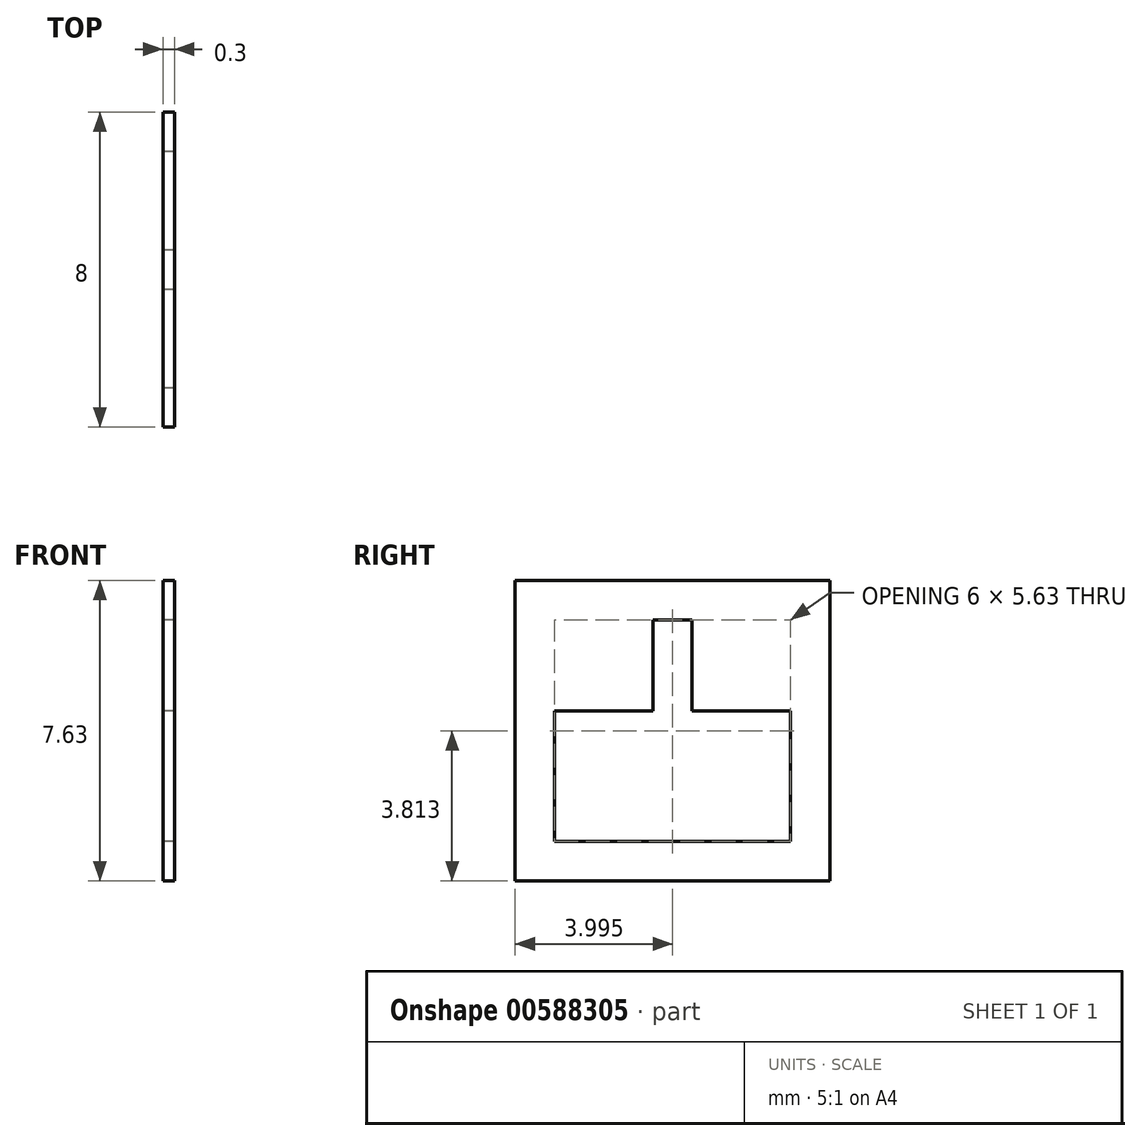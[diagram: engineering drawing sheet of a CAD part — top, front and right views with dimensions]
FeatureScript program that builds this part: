
annotation { "Feature Type Name" : "Feature", "Feature Type Description" : "" }
export const myFeature = defineFeature(function(context is Context, id is Id, definition is map)
    precondition{}
    {
        {
            var Q0;
            Q0=qCreatedBy(makeId("Right.planeOp"),FACE);
            var sketch = newSketch(context, id + "F0", { "sketchPlane" : qUnion([Q0])});
            skLineSegment(sketch, "E0.bottom", {"start": v(-15.22, -11.44) * mm, "end": v(-7.22, -11.44) * mm});
            skLineSegment(sketch, "E0.top", {"start": v(-15.22, -19.07) * mm, "end": v(-7.22, -19.07) * mm});
            skLineSegment(sketch, "E0.left", {"start": v(-15.22, -11.44) * mm, "end": v(-15.22, -19.07) * mm});
            skLineSegment(sketch, "E0.right", {"start": v(-7.22, -11.44) * mm, "end": v(-7.22, -19.07) * mm});
            skLineSegment(sketch, "E1.0", {"start": v(-14.22, -12.44) * mm, "end": v(-8.22, -12.44) * mm});
            skLineSegment(sketch, "E1.1", {"start": v(-14.22, -12.44) * mm, "end": v(-14.22, -18.07) * mm});
            skLineSegment(sketch, "E1.2", {"start": v(-14.22, -18.07) * mm, "end": v(-8.22, -18.07) * mm});
            skLineSegment(sketch, "E1.3", {"start": v(-8.22, -12.44) * mm, "end": v(-8.22, -18.07) * mm});
            skLineSegment(sketch, "E2.bottom", {"start": v(-14.22, -12.44) * mm, "end": v(-11.72, -12.44) * mm});
            skLineSegment(sketch, "E2.top", {"start": v(-14.22, -14.75) * mm, "end": v(-11.72, -14.75) * mm});
            skLineSegment(sketch, "E2.left", {"start": v(-14.22, -12.44) * mm, "end": v(-14.22, -14.75) * mm});
            skLineSegment(sketch, "E2.right", {"start": v(-11.72, -12.44) * mm, "end": v(-11.72, -14.75) * mm});
            skLineSegment(sketch, "E3.bottom", {"start": v(-14.22, -18.07) * mm, "end": v(-11.72, -18.07) * mm});
            skLineSegment(sketch, "E3.top", {"start": v(-14.22, -15.76) * mm, "end": v(-11.72, -15.76) * mm});
            skLineSegment(sketch, "E3.left", {"start": v(-14.22, -18.07) * mm, "end": v(-14.22, -15.76) * mm});
            skLineSegment(sketch, "E3.right", {"start": v(-11.72, -18.07) * mm, "end": v(-11.72, -15.76) * mm});
            skLineSegment(sketch, "E4.bottom", {"start": v(-8.22, -12.44) * mm, "end": v(-10.72, -12.44) * mm});
            skLineSegment(sketch, "E4.top", {"start": v(-8.22, -14.75) * mm, "end": v(-10.72, -14.75) * mm});
            skLineSegment(sketch, "E4.left", {"start": v(-8.22, -12.44) * mm, "end": v(-8.22, -14.75) * mm});
            skLineSegment(sketch, "E4.right", {"start": v(-10.72, -12.44) * mm, "end": v(-10.72, -14.75) * mm});
            skLineSegment(sketch, "E5.bottom", {"start": v(-8.22, -18.07) * mm, "end": v(-10.72, -18.07) * mm});
            skLineSegment(sketch, "E5.top", {"start": v(-8.22, -15.76) * mm, "end": v(-10.72, -15.76) * mm});
            skLineSegment(sketch, "E5.left", {"start": v(-8.22, -18.07) * mm, "end": v(-8.22, -15.76) * mm});
            skLineSegment(sketch, "E5.right", {"start": v(-10.72, -18.07) * mm, "end": v(-10.72, -15.76) * mm});
            skSolve(sketch);
        }
        {
            var Q0;
            Q0=makeQuery(id+"F0.imprint","IMPRINT",FACE,{"disambiguationData":[TD([[makeQuery(id+"F0.imprint","IMPRINT",EDGE,{"derivedFrom":sQuery(id+"F0.wireOp",EDGE,"E0.bottom")}),-1.0]])]});
            var Q1;
            Q1=makeQuery(id+"F0.imprint","IMPRINT",FACE,{"disambiguationData":[TD([[makeQuery(id+"F0.imprint","IMPRINT",EDGE,{"derivedFrom":sQuery(id+"F0.wireOp",EDGE,"E1.0")}),-1.0]])]});
            extrude(context, id + "F1", {"entities" : qUnion([Q0, Q1]), "depth" : .3 * mm, "offsetDistance" : 25 * mm});
        }
    });
